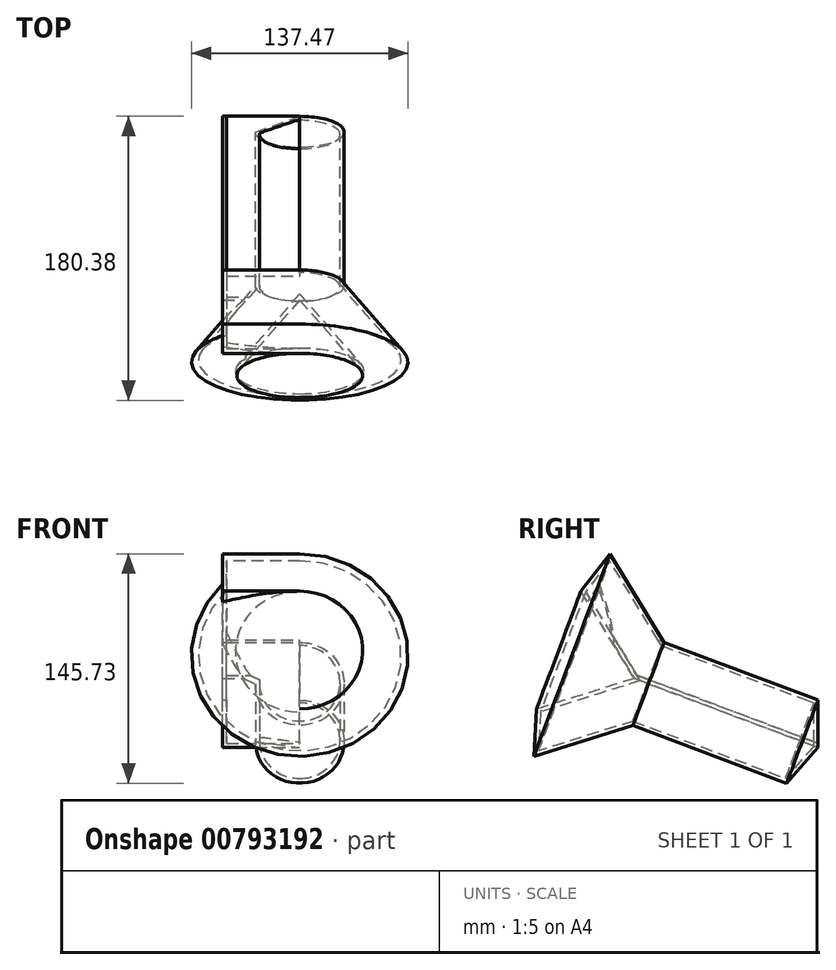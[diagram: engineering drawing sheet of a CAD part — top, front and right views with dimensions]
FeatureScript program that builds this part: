
annotation { "Feature Type Name" : "Feature", "Feature Type Description" : "" }
export const myFeature = defineFeature(function(context is Context, id is Id, definition is map)
    precondition{}
    {
        {
            var Q0;
            Q0=qCreatedBy(makeId("Front.planeOp"),FACE);
            var sketch = newSketch(context, id + "F0", { "sketchPlane" : qUnion([Q0])});
            skLineSegment(sketch, "E0.bottom", {"start": v(0, 0) * mm, "end": v(48.88, 0) * mm});
            skLineSegment(sketch, "E0.top", {"start": v(0, 30.13) * mm, "end": v(48.88, 30.13) * mm});
            skLineSegment(sketch, "E0.left", {"start": v(0, 0) * mm, "end": v(0, 30.13) * mm});
            skLineSegment(sketch, "E0.right", {"start": v(48.88, 0) * mm, "end": v(48.88, 30.13) * mm});
            skLineSegment(sketch, "E1", {"start": v(-18.36, 52.18) * mm, "end": v(94.43, 36.5) * mm, "construction": true});
            skSolve(sketch);
        }
        {
            var Q0;
            Q0=qCreatedBy(makeId("Right.planeOp"),FACE);
            var sketch = newSketch(context, id + "F1", { "sketchPlane" : qUnion([Q0])});
            skLineSegment(sketch, "E2", {"start": v(0, 0) * mm, "end": v(-116.65, 43.85) * mm});
            skLineSegment(sketch, "E3", {"start": v(-116.65, 43.85) * mm, "end": v(-150.54, 99.3) * mm});
            skSolve(sketch);
        }
        {
            var Q0;
            Q0=makeQuery(id+"F0.imprint","IMPRINT",FACE,{"disambiguationData":[TD([[makeQuery(id+"F0.imprint","IMPRINT",EDGE,{"derivedFrom":sQuery(id+"F0.wireOp",EDGE,"E0.bottom")}),1.0]])]});
            var Q1;
            Q1=sQuery(id+"F1.wireOp",EDGE,"E2");
            var Q2;
            Q2=sQuery(id+"F1.wireOp",EDGE,"E3");
            sweep(context, id + "F2", {"profiles" : qUnion([Q0]), "path" : qUnion([Q1, Q2])});
        }
        {
            var Q0;
            Q0=makeQuery(id+"F2.opSweep","SWEPT_FACE",FACE,{"disambiguationData":[OSD([sQuery(id+"F0.wireOp",EDGE,"E0.right"),sQuery(id+"F1.wireOp",EDGE,"E2")])]});
            var Q1;
            Q1=makeQuery(id+"F2.opSweep","SWEPT_EDGE",EDGE,{"disambiguationData":[OSD([sQuery(id+"F0.wireOp",EDGE,"E0.bottom"),sQuery(id+"F0.wireOp",EDGE,"E0.right"),sQuery(id+"F1.wireOp",EDGE,"E2")])]});
            revolve(context, id + "F3", {"operationType" : NewBodyOperationType.ADD, "surfaceOperationType" : NewSurfaceOperationType.NEW, "entities" : qUnion([Q0]), "axis" : qUnion([Q1]), "revolveType" : RevolveType.FULL});
        }
        {
            var Q0;
            Q0=makeQuery(id+"F2.opSweep","CAP_FACE",FACE,{"disambiguationData":[OSD([sQuery(id+"F0.wireOp",EDGE,"E0.bottom"),sQuery(id+"F0.wireOp",EDGE,"E0.top"),sQuery(id+"F0.wireOp",EDGE,"E0.left"),sQuery(id+"F0.wireOp",EDGE,"E0.right"),sQuery(id+"F1.wireOp",VERTEX,"E2.start")])],"isStart":true});
            var Q1;
            Q1=makeQuery(id+"F2.opSweep","SWEPT_FACE",FACE,{"disambiguationData":[OSD([sQuery(id+"F0.wireOp",EDGE,"E0.top"),sQuery(id+"F1.wireOp",EDGE,"E2")])]});
            shell(context, id + "F4", {"entities" : qUnion([Q0, Q1]), "thickness" : 2.54 * mm});
        }
    });
